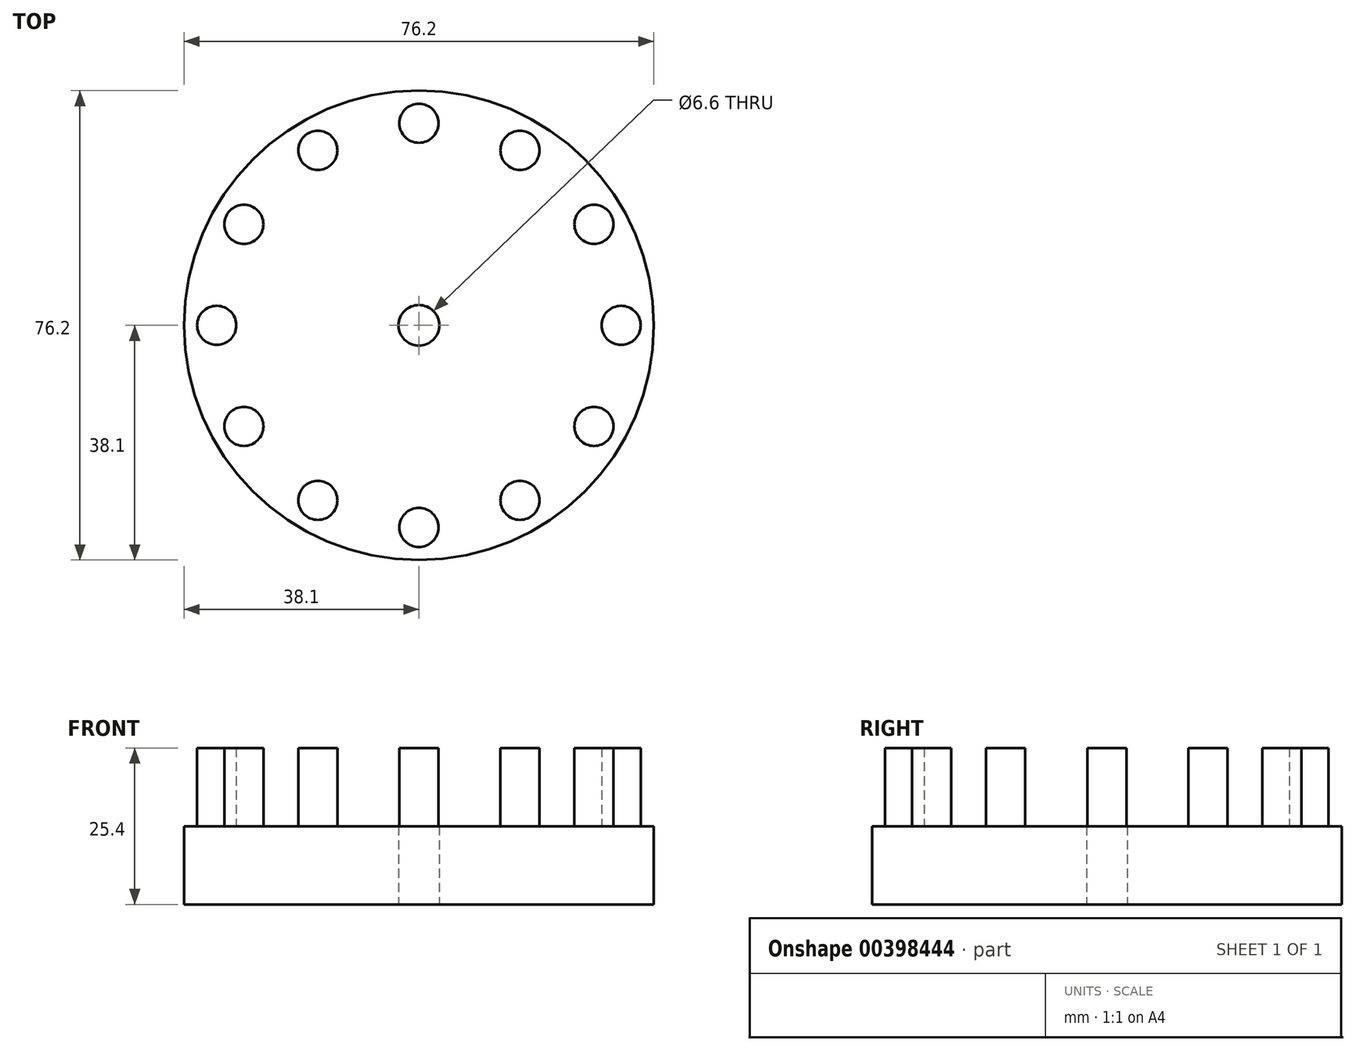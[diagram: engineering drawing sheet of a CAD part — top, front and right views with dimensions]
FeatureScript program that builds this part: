
annotation { "Feature Type Name" : "Feature", "Feature Type Description" : "" }
export const myFeature = defineFeature(function(context is Context, id is Id, definition is map)
    precondition{}
    {
        {
            var Q0;
            Q0=qCreatedBy(makeId("Top.planeOp"),FACE);
            var sketch = newSketch(context, id + "F0", { "sketchPlane" : qUnion([Q0])});
            skCircle(sketch, "E0", {"center": v(0, 0) * mm, "radius": 38.1 * mm});
            skPoint(sketch, "E1.orphan", {"position": v(0, 38.1) * mm});
            skCircle(sketch, "E2", {"center": v(0, 0) * mm, "radius": 3.3 * mm});
            skSolve(sketch);
        }
        {
            var Q0;
            Q0 = qSketchRegion(id + "F0", true);
            extrude(context, id + "F1", {"entities" : qUnion([Q0]), "depth" : 12.7 * mm});
        }
        {
            var Q0;
            Q0=makeQuery(id+"F1.opExtrude","CAP_FACE",FACE,{"disambiguationData":[OSD([sQuery(id+"F0.wireOp",EDGE,"E0"),sQuery(id+"F0.wireOp",EDGE,"E2")])],"isStart":false});
            var sketch = newSketch(context, id + "F2", { "sketchPlane" : qUnion([Q0])});
            skCircle(sketch, "E3", {"center": v(0, 32.8) * mm, "radius": 3.18 * mm});
            skPoint(sketch, "E4.orphan", {"position": v(0, 38.1) * mm});
            skCircle(sketch, "E5.1.0", {"center": v(-16.4, 28.4) * mm, "radius": 3.18 * mm});
            skCircle(sketch, "E5.2.0", {"center": v(-28.4, 16.4) * mm, "radius": 3.18 * mm});
            skCircle(sketch, "E5.3.0", {"center": v(-32.8, 0) * mm, "radius": 3.18 * mm});
            skCircle(sketch, "E5.4.0", {"center": v(-28.4, -16.4) * mm, "radius": 3.18 * mm});
            skCircle(sketch, "E5.5.0", {"center": v(-16.4, -28.4) * mm, "radius": 3.18 * mm});
            skCircle(sketch, "E5.6.0", {"center": v(0, -32.8) * mm, "radius": 3.18 * mm});
            skCircle(sketch, "E5.7.0", {"center": v(16.4, -28.4) * mm, "radius": 3.18 * mm});
            skCircle(sketch, "E5.8.0", {"center": v(28.4, -16.4) * mm, "radius": 3.18 * mm});
            skCircle(sketch, "E5.9.0", {"center": v(32.8, 0) * mm, "radius": 3.18 * mm});
            skCircle(sketch, "E5.10.0", {"center": v(28.4, 16.4) * mm, "radius": 3.18 * mm});
            skCircle(sketch, "E5.11.0", {"center": v(16.4, 28.4) * mm, "radius": 3.18 * mm});
            skPoint(sketch, "E5.center", {"position": v(0, 0) * mm});
            skSolve(sketch);
        }
        {
            var Q0;
            Q0 = qSketchRegion(id + "F2", true);
            extrude(context, id + "F3", {"entities" : qUnion([Q0]), "operationType" : NewBodyOperationType.ADD, "depth" : 12.7 * mm});
        }
    });
